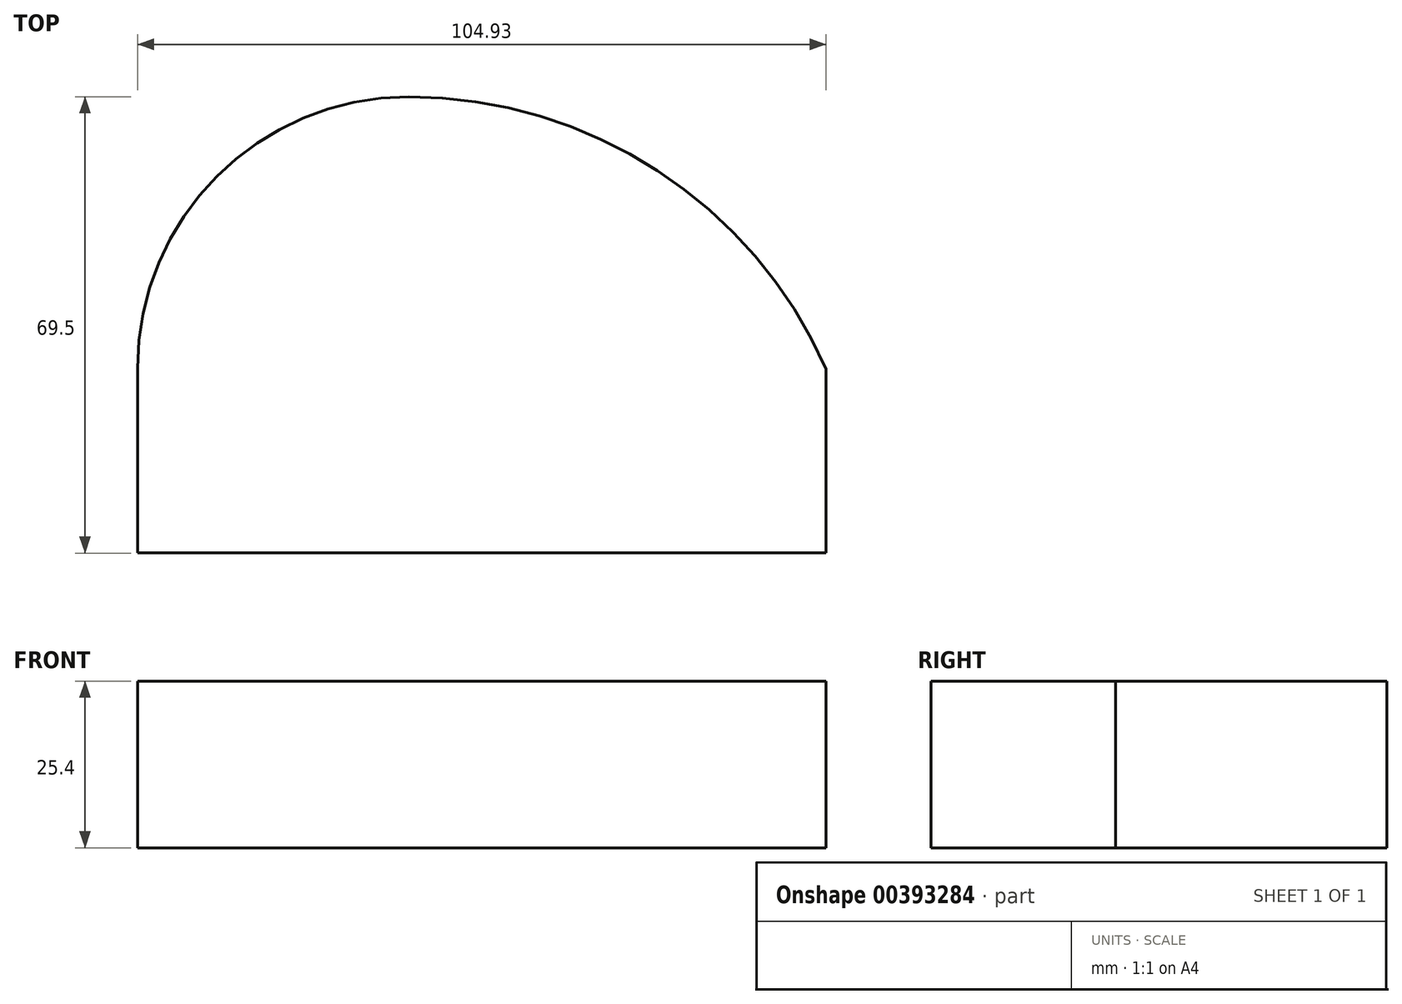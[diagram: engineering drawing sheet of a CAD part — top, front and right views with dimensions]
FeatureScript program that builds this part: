
annotation { "Feature Type Name" : "Feature", "Feature Type Description" : "" }
export const myFeature = defineFeature(function(context is Context, id is Id, definition is map)
    precondition{}
    {
        {
            var Q0;
            Q0=qCreatedBy(makeId("Top.planeOp"),FACE);
            var sketch = newSketch(context, id + "F0", { "sketchPlane" : qUnion([Q0])});
            skArc(sketch, "E0", {"start": v(-41.34, 0) * mm, "mid": v(-29.23, 29.23) * mm, "end": v(0, 41.34) * mm});
            skArc(sketch, "E1", {"start": v(0, 41.34) * mm, "mid": v(37.9, 30.1) * mm, "end": v(63.54, 0) * mm});
            skLineSegment(sketch, "E2.bottom", {"start": v(-41.34, 0) * mm, "end": v(63.6, 0) * mm});
            skLineSegment(sketch, "E2.top", {"start": v(-41.34, -28.16) * mm, "end": v(63.6, -28.16) * mm});
            skLineSegment(sketch, "E2.left", {"start": v(-41.34, 0) * mm, "end": v(-41.34, -28.16) * mm});
            skLineSegment(sketch, "E2.right", {"start": v(63.6, 0) * mm, "end": v(63.6, -28.16) * mm});
            skSolve(sketch);
        }
        {
            var Q0;
            Q0 = qSketchRegion(id + "F0", true);
            extrude(context, id + "F1", {"entities" : qUnion([Q0]), "depth" : 25.4 * mm, "offsetDistance" : 25.4 * mm});
        }
    });
